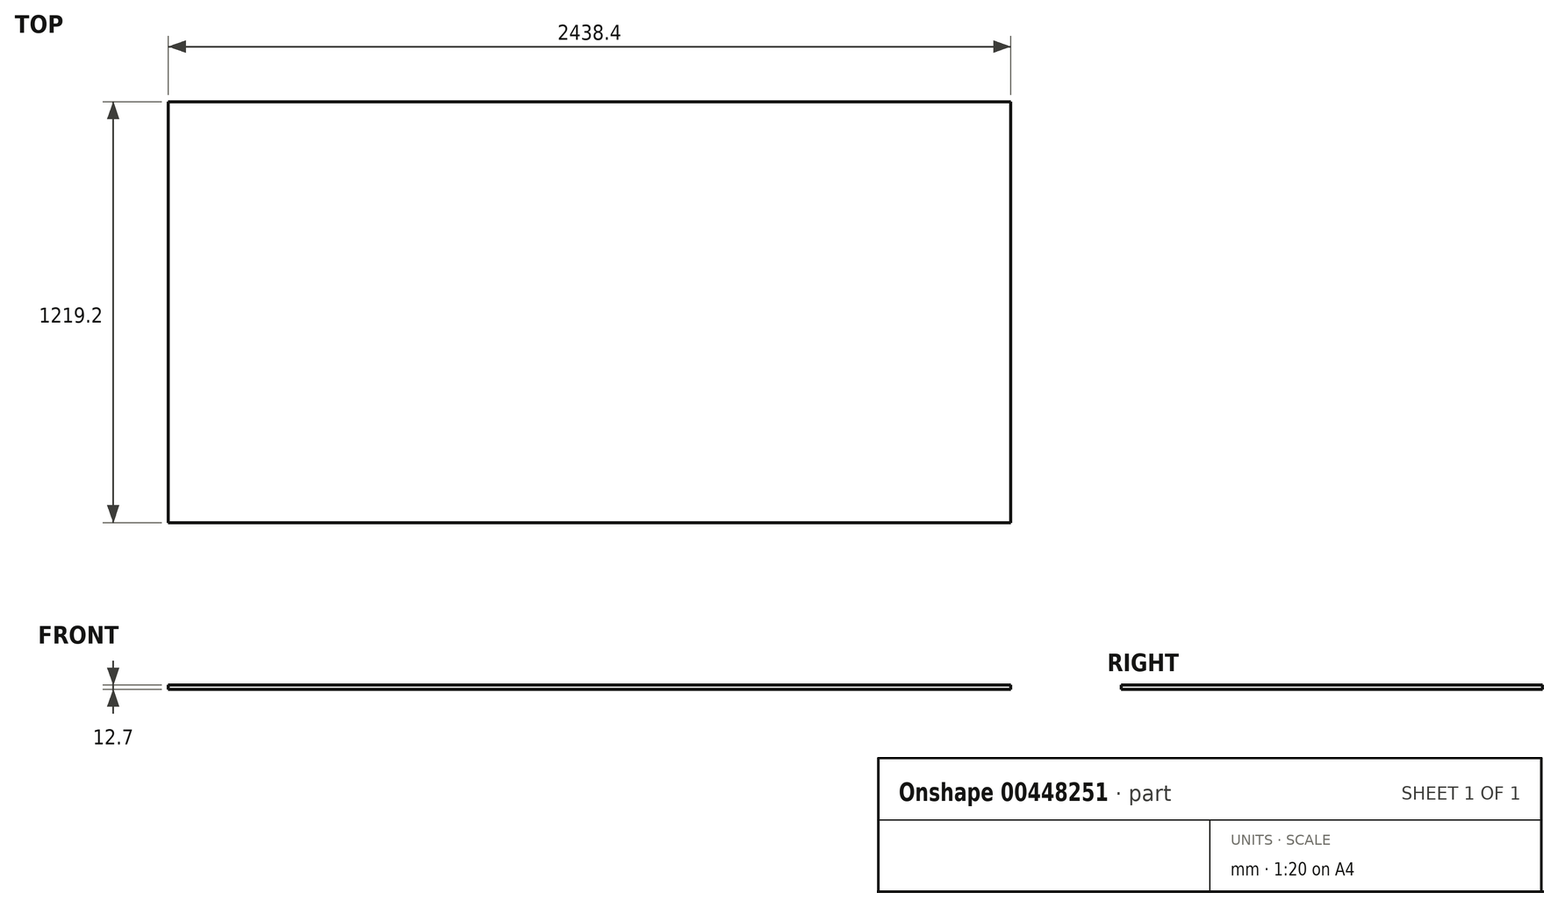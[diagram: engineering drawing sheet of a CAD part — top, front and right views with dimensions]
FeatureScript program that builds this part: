
annotation { "Feature Type Name" : "Feature", "Feature Type Description" : "" }
export const myFeature = defineFeature(function(context is Context, id is Id, definition is map)
    precondition{}
    {
        {
            var Q0;
            Q0=qCreatedBy(makeId("Top.planeOp"),FACE);
            var sketch = newSketch(context, id + "F0", { "sketchPlane" : qUnion([Q0])});
            skLineSegment(sketch, "E0.bottom", {"start": v(-1219.2, 609.6) * mm, "end": v(1219.2, 609.6) * mm});
            skLineSegment(sketch, "E0.top", {"start": v(-1219.2, -609.6) * mm, "end": v(1219.2, -609.6) * mm});
            skLineSegment(sketch, "E0.left", {"start": v(-1219.2, 609.6) * mm, "end": v(-1219.2, -609.6) * mm});
            skLineSegment(sketch, "E0.right", {"start": v(1219.2, 609.6) * mm, "end": v(1219.2, -609.6) * mm});
            skSolve(sketch);
        }
        {
            var Q0;
            Q0=qSketchRegion(id+"F0",true);
            extrude(context, id + "F1", {"entities" : qUnion([Q0]), "depth" : 12.7 * mm});
        }
    });
